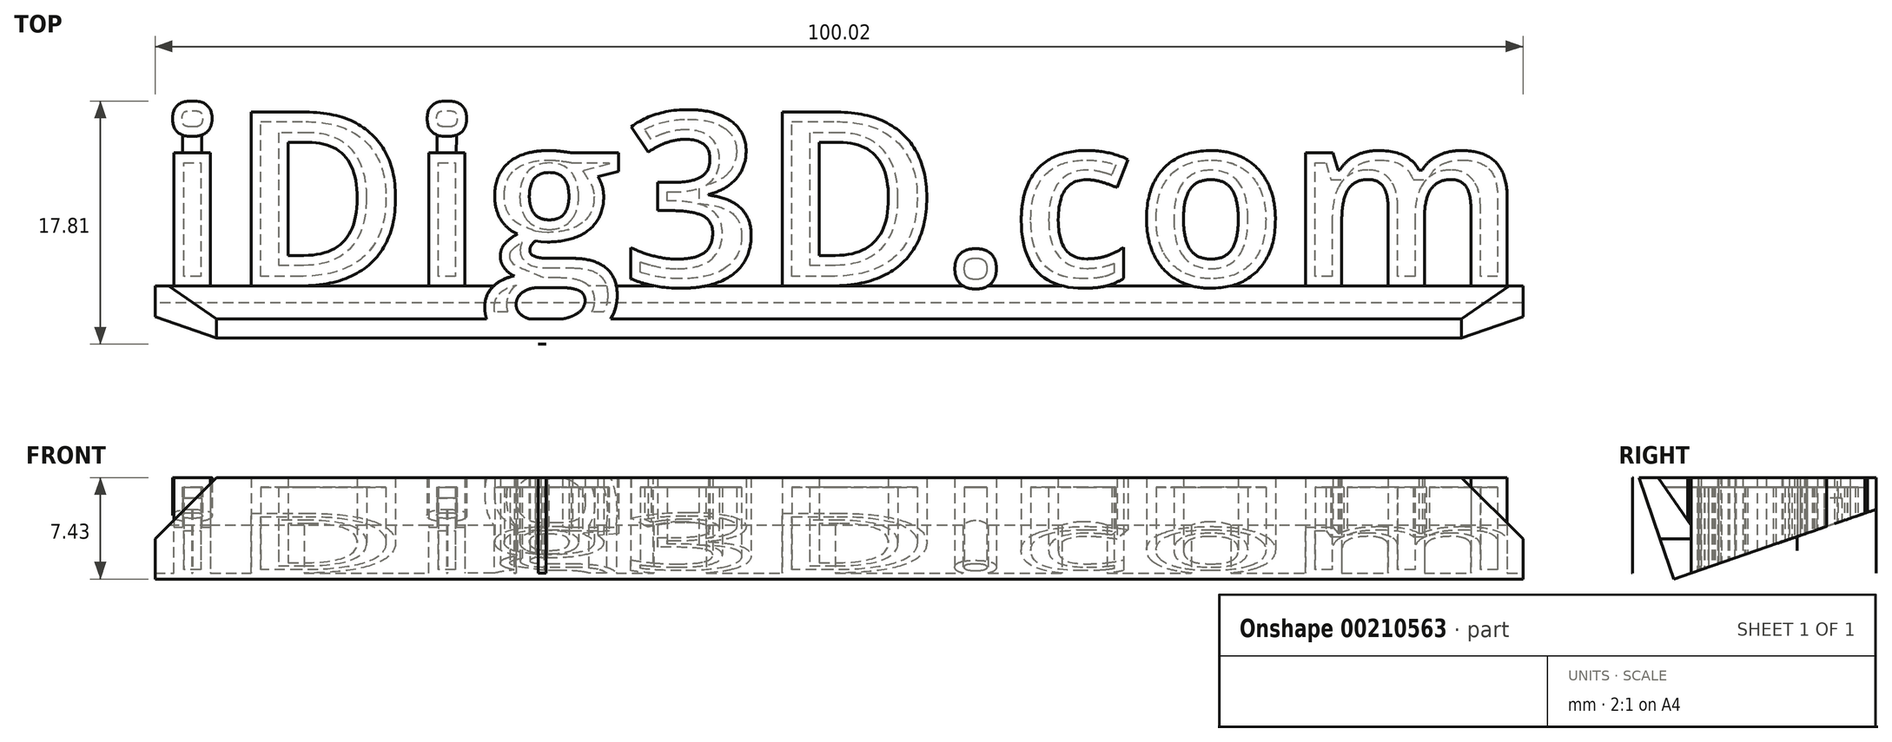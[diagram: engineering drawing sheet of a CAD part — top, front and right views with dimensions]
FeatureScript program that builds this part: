
annotation { "Feature Type Name" : "Feature", "Feature Type Description" : "" }
export const myFeature = defineFeature(function(context is Context, id is Id, definition is map)
    precondition{}
    {
        {
            var Q0;
            Q0=qCreatedBy(makeId("Top.planeOp"),FACE);
            var sketch = newSketch(context, id + "F0", { "sketchPlane" : qUnion([Q0])});
            skText(sketch, "E0", { "text": "iDig3D.com", "fontName": "OpenSans-Bold.ttf"});
            const initialGuessF0  = {"E0": [-0.05, -0.01282, 1, 0, 0.01282]};
            skSetInitialGuess(sketch, initialGuessF0);
            skSolve(sketch);
        }
        {
            var Q0;
            Q0=qSketchRegion(id+"F0",true);
            extrude(context, id + "F1", {"entities" : qUnion([Q0]), "depth" : 7 * mm});
        }
        {
            var Q0;
            Q0=makeQuery(id+"F0.imprint","IMPRINT",FACE,{"disambiguationData":[TD([[makeQuery(id+"F0.imprint","IMPRINT",EDGE,{"derivedFrom":sQuery(id+"F0.wireOp",EDGE,"E0.sketch_text.stroke-5")}),-1.0]])]});
            var sketch = newSketch(context, id + "F2", { "sketchPlane" : qUnion([Q0])});
            skPoint(sketch, "E1.0", {"position": v(-47.28, -3.1) * mm});
            skPoint(sketch, "E2.0", {"position": v(-28.67, -3.1) * mm});
            skPoint(sketch, "E3.0", {"position": v(-28.67, -1.9) * mm});
            skPoint(sketch, "E4.0", {"position": v(-47.28, -1.9) * mm});
            skLineSegment(sketch, "E5", {"start": v(-28.67, -1.9) * mm, "end": v(-28.67, -3.1) * mm});
            skLineSegment(sketch, "E6", {"start": v(-47.28, -1.9) * mm, "end": v(-47.28, -3.1) * mm});
            skArc(sketch, "E7.0.startCap", {"start": v(-29.37, -1.89) * mm, "mid": v(-28.67, -1.2) * mm, "end": v(-27.97, -1.9) * mm});
            skArc(sketch, "E7.0.endCap", {"start": v(-27.97, -3.1) * mm, "mid": v(-28.67, -3.8) * mm, "end": v(-29.37, -3.1) * mm});
            skLineSegment(sketch, "E7.0.left", {"start": v(-27.97, -1.9) * mm, "end": v(-27.97, -3.1) * mm});
            skLineSegment(sketch, "E7.0.right", {"start": v(-29.37, -1.89) * mm, "end": v(-29.37, -3.1) * mm});
            skArc(sketch, "E7.1.startCap", {"start": v(-47.98, -1.89) * mm, "mid": v(-47.28, -1.2) * mm, "end": v(-46.58, -1.9) * mm});
            skArc(sketch, "E7.1.endCap", {"start": v(-46.58, -3.1) * mm, "mid": v(-47.29, -3.8) * mm, "end": v(-47.98, -3.1) * mm});
            skLineSegment(sketch, "E7.1.left", {"start": v(-46.58, -1.9) * mm, "end": v(-46.58, -3.1) * mm});
            skLineSegment(sketch, "E7.1.right", {"start": v(-47.98, -1.89) * mm, "end": v(-47.98, -3.1) * mm});
            skSolve(sketch);
        }
        {
            var Q0;
            Q0=qSketchRegion(id+"F2",true);
            extrude(context, id + "F3", {"entities" : qUnion([Q0]), "operationType" : NewBodyOperationType.ADD, "depth" : 5.5 * mm});
        }
        {
            var Q0;
            Q0=makeQuery(id+"F1.opExtrude","CAP_FACE",FACE,{"disambiguationData":[OSD([sQuery(id+"F0.wireOp",EDGE,"E0.sketch_text.stroke-153"),sQuery(id+"F0.wireOp",EDGE,"E0.sketch_text.stroke-154"),sQuery(id+"F0.wireOp",EDGE,"E0.sketch_text.stroke-155"),sQuery(id+"F0.wireOp",EDGE,"E0.sketch_text.stroke-156"),sQuery(id+"F0.wireOp",EDGE,"E0.sketch_text.stroke-157"),sQuery(id+"F0.wireOp",EDGE,"E0.sketch_text.stroke-158"),sQuery(id+"F0.wireOp",EDGE,"E0.sketch_text.stroke-159"),sQuery(id+"F0.wireOp",EDGE,"E0.sketch_text.stroke-160"),sQuery(id+"F0.wireOp",EDGE,"E0.sketch_text.stroke-161"),sQuery(id+"F0.wireOp",EDGE,"E0.sketch_text.stroke-162"),sQuery(id+"F0.wireOp",EDGE,"E0.sketch_text.stroke-163"),sQuery(id+"F0.wireOp",EDGE,"E0.sketch_text.stroke-164"),sQuery(id+"F0.wireOp",EDGE,"E0.sketch_text.stroke-165"),sQuery(id+"F0.wireOp",EDGE,"E0.sketch_text.stroke-166"),sQuery(id+"F0.wireOp",EDGE,"E0.sketch_text.stroke-167"),sQuery(id+"F0.wireOp",EDGE,"E0.sketch_text.stroke-168"),sQuery(id+"F0.wireOp",EDGE,"E0.sketch_text.stroke-169"),sQuery(id+"F0.wireOp",EDGE,"E0.sketch_text.stroke-170"),sQuery(id+"F0.wireOp",EDGE,"E0.sketch_text.stroke-171"),sQuery(id+"F0.wireOp",EDGE,"E0.sketch_text.stroke-172"),sQuery(id+"F0.wireOp",EDGE,"E0.sketch_text.stroke-173"),sQuery(id+"F0.wireOp",EDGE,"E0.sketch_text.stroke-174"),sQuery(id+"F0.wireOp",EDGE,"E0.sketch_text.stroke-175"),sQuery(id+"F0.wireOp",EDGE,"E0.sketch_text.stroke-176"),sQuery(id+"F0.wireOp",EDGE,"E0.sketch_text.stroke-177"),sQuery(id+"F0.wireOp",EDGE,"E0.sketch_text.stroke-178"),sQuery(id+"F0.wireOp",EDGE,"E0.sketch_text.stroke-179"),sQuery(id+"F0.wireOp",EDGE,"E0.sketch_text.stroke-180")])],"isStart":true});
            var Q1;
            Q1=makeQuery(id+"F1.opExtrude","CAP_FACE",FACE,{"disambiguationData":[OSD([sQuery(id+"F0.wireOp",EDGE,"E0.sketch_text.stroke-30"),sQuery(id+"F0.wireOp",EDGE,"E0.sketch_text.stroke-31"),sQuery(id+"F0.wireOp",EDGE,"E0.sketch_text.stroke-32"),sQuery(id+"F0.wireOp",EDGE,"E0.sketch_text.stroke-33"),sQuery(id+"F0.wireOp",EDGE,"E0.sketch_text.stroke-34"),sQuery(id+"F0.wireOp",EDGE,"E0.sketch_text.stroke-35"),sQuery(id+"F0.wireOp",EDGE,"E0.sketch_text.stroke-36"),sQuery(id+"F0.wireOp",EDGE,"E0.sketch_text.stroke-37"),sQuery(id+"F0.wireOp",EDGE,"E0.sketch_text.stroke-38"),sQuery(id+"F0.wireOp",EDGE,"E0.sketch_text.stroke-39"),sQuery(id+"F0.wireOp",EDGE,"E0.sketch_text.stroke-40"),sQuery(id+"F0.wireOp",EDGE,"E0.sketch_text.stroke-41"),sQuery(id+"F0.wireOp",EDGE,"E0.sketch_text.stroke-42"),sQuery(id+"F0.wireOp",EDGE,"E0.sketch_text.stroke-43"),sQuery(id+"F0.wireOp",EDGE,"E0.sketch_text.stroke-44"),sQuery(id+"F0.wireOp",EDGE,"E0.sketch_text.stroke-45"),sQuery(id+"F0.wireOp",EDGE,"E0.sketch_text.stroke-46"),sQuery(id+"F0.wireOp",EDGE,"E0.sketch_text.stroke-47"),sQuery(id+"F0.wireOp",EDGE,"E0.sketch_text.stroke-48"),sQuery(id+"F0.wireOp",EDGE,"E0.sketch_text.stroke-49"),sQuery(id+"F0.wireOp",EDGE,"E0.sketch_text.stroke-50"),sQuery(id+"F0.wireOp",EDGE,"E0.sketch_text.stroke-51"),sQuery(id+"F0.wireOp",EDGE,"E0.sketch_text.stroke-52"),sQuery(id+"F0.wireOp",EDGE,"E0.sketch_text.stroke-53"),sQuery(id+"F0.wireOp",EDGE,"E0.sketch_text.stroke-54"),sQuery(id+"F0.wireOp",EDGE,"E0.sketch_text.stroke-55"),sQuery(id+"F0.wireOp",EDGE,"E0.sketch_text.stroke-56"),sQuery(id+"F0.wireOp",EDGE,"E0.sketch_text.stroke-57"),sQuery(id+"F0.wireOp",EDGE,"E0.sketch_text.stroke-58"),sQuery(id+"F0.wireOp",EDGE,"E0.sketch_text.stroke-59"),sQuery(id+"F0.wireOp",EDGE,"E0.sketch_text.stroke-60"),sQuery(id+"F0.wireOp",EDGE,"E0.sketch_text.stroke-61"),sQuery(id+"F0.wireOp",EDGE,"E0.sketch_text.stroke-62"),sQuery(id+"F0.wireOp",EDGE,"E0.sketch_text.stroke-63"),sQuery(id+"F0.wireOp",EDGE,"E0.sketch_text.stroke-64"),sQuery(id+"F0.wireOp",EDGE,"E0.sketch_text.stroke-65"),sQuery(id+"F0.wireOp",EDGE,"E0.sketch_text.stroke-66"),sQuery(id+"F0.wireOp",EDGE,"E0.sketch_text.stroke-67"),sQuery(id+"F0.wireOp",EDGE,"E0.sketch_text.stroke-68"),sQuery(id+"F0.wireOp",EDGE,"E0.sketch_text.stroke-69"),sQuery(id+"F0.wireOp",EDGE,"E0.sketch_text.stroke-70"),sQuery(id+"F0.wireOp",EDGE,"E0.sketch_text.stroke-71"),sQuery(id+"F0.wireOp",EDGE,"E0.sketch_text.stroke-72"),sQuery(id+"F0.wireOp",EDGE,"E0.sketch_text.stroke-73")])],"isStart":true});
            var Q2;
            Q2=makeQuery(id+"F1.opExtrude","CAP_FACE",FACE,{"disambiguationData":[OSD([sQuery(id+"F0.wireOp",EDGE,"E0.sketch_text.stroke-101"),sQuery(id+"F0.wireOp",EDGE,"E0.sketch_text.stroke-102"),sQuery(id+"F0.wireOp",EDGE,"E0.sketch_text.stroke-103"),sQuery(id+"F0.wireOp",EDGE,"E0.sketch_text.stroke-104"),sQuery(id+"F0.wireOp",EDGE,"E0.sketch_text.stroke-105"),sQuery(id+"F0.wireOp",EDGE,"E0.sketch_text.stroke-106"),sQuery(id+"F0.wireOp",EDGE,"E0.sketch_text.stroke-107"),sQuery(id+"F0.wireOp",EDGE,"E0.sketch_text.stroke-108"),sQuery(id+"F0.wireOp",EDGE,"E0.sketch_text.stroke-109"),sQuery(id+"F0.wireOp",EDGE,"E0.sketch_text.stroke-110"),sQuery(id+"F0.wireOp",EDGE,"E0.sketch_text.stroke-111"),sQuery(id+"F0.wireOp",EDGE,"E0.sketch_text.stroke-112")])],"isStart":true});
            var Q3;
            Q3=makeQuery(id+"F1.opExtrude","CAP_FACE",FACE,{"disambiguationData":[OSD([sQuery(id+"F0.wireOp",EDGE,"E0.sketch_text.stroke-0"),sQuery(id+"F0.wireOp",EDGE,"E0.sketch_text.stroke-1"),sQuery(id+"F0.wireOp",EDGE,"E0.sketch_text.stroke-2"),sQuery(id+"F0.wireOp",EDGE,"E0.sketch_text.stroke-3"),sQuery(id+"F0.wireOp",EDGE,"E0.sketch_text.stroke-4")])],"isStart":true});
            var Q4;
            Q4=makeQuery(id+"F1.opExtrude","CAP_FACE",FACE,{"disambiguationData":[OSD([sQuery(id+"F0.wireOp",EDGE,"E0.sketch_text.stroke-135"),sQuery(id+"F0.wireOp",EDGE,"E0.sketch_text.stroke-136"),sQuery(id+"F0.wireOp",EDGE,"E0.sketch_text.stroke-137"),sQuery(id+"F0.wireOp",EDGE,"E0.sketch_text.stroke-138"),sQuery(id+"F0.wireOp",EDGE,"E0.sketch_text.stroke-139"),sQuery(id+"F0.wireOp",EDGE,"E0.sketch_text.stroke-140"),sQuery(id+"F0.wireOp",EDGE,"E0.sketch_text.stroke-141"),sQuery(id+"F0.wireOp",EDGE,"E0.sketch_text.stroke-142"),sQuery(id+"F0.wireOp",EDGE,"E0.sketch_text.stroke-143"),sQuery(id+"F0.wireOp",EDGE,"E0.sketch_text.stroke-144"),sQuery(id+"F0.wireOp",EDGE,"E0.sketch_text.stroke-145"),sQuery(id+"F0.wireOp",EDGE,"E0.sketch_text.stroke-146"),sQuery(id+"F0.wireOp",EDGE,"E0.sketch_text.stroke-147"),sQuery(id+"F0.wireOp",EDGE,"E0.sketch_text.stroke-148"),sQuery(id+"F0.wireOp",EDGE,"E0.sketch_text.stroke-149"),sQuery(id+"F0.wireOp",EDGE,"E0.sketch_text.stroke-150"),sQuery(id+"F0.wireOp",EDGE,"E0.sketch_text.stroke-151"),sQuery(id+"F0.wireOp",EDGE,"E0.sketch_text.stroke-152")])],"isStart":true});
            var Q5;
            Q5=makeQuery(id+"F1.opExtrude","CAP_FACE",FACE,{"disambiguationData":[OSD([sQuery(id+"F0.wireOp",EDGE,"E0.sketch_text.stroke-121"),sQuery(id+"F0.wireOp",EDGE,"E0.sketch_text.stroke-122"),sQuery(id+"F0.wireOp",EDGE,"E0.sketch_text.stroke-123"),sQuery(id+"F0.wireOp",EDGE,"E0.sketch_text.stroke-124"),sQuery(id+"F0.wireOp",EDGE,"E0.sketch_text.stroke-125"),sQuery(id+"F0.wireOp",EDGE,"E0.sketch_text.stroke-126"),sQuery(id+"F0.wireOp",EDGE,"E0.sketch_text.stroke-127"),sQuery(id+"F0.wireOp",EDGE,"E0.sketch_text.stroke-128"),sQuery(id+"F0.wireOp",EDGE,"E0.sketch_text.stroke-129"),sQuery(id+"F0.wireOp",EDGE,"E0.sketch_text.stroke-130"),sQuery(id+"F0.wireOp",EDGE,"E0.sketch_text.stroke-131"),sQuery(id+"F0.wireOp",EDGE,"E0.sketch_text.stroke-132"),sQuery(id+"F0.wireOp",EDGE,"E0.sketch_text.stroke-133"),sQuery(id+"F0.wireOp",EDGE,"E0.sketch_text.stroke-134")])],"isStart":true});
            var Q6;
            Q6=makeQuery(id+"F1.opExtrude","CAP_FACE",FACE,{"disambiguationData":[OSD([sQuery(id+"F0.wireOp",EDGE,"E0.sketch_text.stroke-74"),sQuery(id+"F0.wireOp",EDGE,"E0.sketch_text.stroke-75"),sQuery(id+"F0.wireOp",EDGE,"E0.sketch_text.stroke-76"),sQuery(id+"F0.wireOp",EDGE,"E0.sketch_text.stroke-77"),sQuery(id+"F0.wireOp",EDGE,"E0.sketch_text.stroke-78"),sQuery(id+"F0.wireOp",EDGE,"E0.sketch_text.stroke-79"),sQuery(id+"F0.wireOp",EDGE,"E0.sketch_text.stroke-80"),sQuery(id+"F0.wireOp",EDGE,"E0.sketch_text.stroke-81"),sQuery(id+"F0.wireOp",EDGE,"E0.sketch_text.stroke-82"),sQuery(id+"F0.wireOp",EDGE,"E0.sketch_text.stroke-83"),sQuery(id+"F0.wireOp",EDGE,"E0.sketch_text.stroke-84"),sQuery(id+"F0.wireOp",EDGE,"E0.sketch_text.stroke-85"),sQuery(id+"F0.wireOp",EDGE,"E0.sketch_text.stroke-86"),sQuery(id+"F0.wireOp",EDGE,"E0.sketch_text.stroke-87"),sQuery(id+"F0.wireOp",EDGE,"E0.sketch_text.stroke-88"),sQuery(id+"F0.wireOp",EDGE,"E0.sketch_text.stroke-89"),sQuery(id+"F0.wireOp",EDGE,"E0.sketch_text.stroke-90"),sQuery(id+"F0.wireOp",EDGE,"E0.sketch_text.stroke-91"),sQuery(id+"F0.wireOp",EDGE,"E0.sketch_text.stroke-92"),sQuery(id+"F0.wireOp",EDGE,"E0.sketch_text.stroke-93"),sQuery(id+"F0.wireOp",EDGE,"E0.sketch_text.stroke-94"),sQuery(id+"F0.wireOp",EDGE,"E0.sketch_text.stroke-95"),sQuery(id+"F0.wireOp",EDGE,"E0.sketch_text.stroke-96"),sQuery(id+"F0.wireOp",EDGE,"E0.sketch_text.stroke-97"),sQuery(id+"F0.wireOp",EDGE,"E0.sketch_text.stroke-98"),sQuery(id+"F0.wireOp",EDGE,"E0.sketch_text.stroke-99"),sQuery(id+"F0.wireOp",EDGE,"E0.sketch_text.stroke-100")])],"isStart":true});
            var Q7;
            Q7=makeQuery(id+"F1.opExtrude","CAP_FACE",FACE,{"disambiguationData":[OSD([sQuery(id+"F0.wireOp",EDGE,"E0.sketch_text.stroke-21"),sQuery(id+"F0.wireOp",EDGE,"E0.sketch_text.stroke-22"),sQuery(id+"F0.wireOp",EDGE,"E0.sketch_text.stroke-23"),sQuery(id+"F0.wireOp",EDGE,"E0.sketch_text.stroke-24"),sQuery(id+"F0.wireOp",EDGE,"E0.sketch_text.stroke-25")])],"isStart":true});
            var Q8;
            Q8=makeQuery(id+"F1.opExtrude","CAP_FACE",FACE,{"disambiguationData":[OSD([sQuery(id+"F0.wireOp",EDGE,"E0.sketch_text.stroke-26"),sQuery(id+"F0.wireOp",EDGE,"E0.sketch_text.stroke-27"),sQuery(id+"F0.wireOp",EDGE,"E0.sketch_text.stroke-28"),sQuery(id+"F0.wireOp",EDGE,"E0.sketch_text.stroke-29")])],"isStart":true});
            var Q9;
            Q9=makeQuery(id+"F1.opExtrude","CAP_FACE",FACE,{"disambiguationData":[OSD([sQuery(id+"F0.wireOp",EDGE,"E0.sketch_text.stroke-9"),sQuery(id+"F0.wireOp",EDGE,"E0.sketch_text.stroke-10"),sQuery(id+"F0.wireOp",EDGE,"E0.sketch_text.stroke-11"),sQuery(id+"F0.wireOp",EDGE,"E0.sketch_text.stroke-12"),sQuery(id+"F0.wireOp",EDGE,"E0.sketch_text.stroke-13"),sQuery(id+"F0.wireOp",EDGE,"E0.sketch_text.stroke-14"),sQuery(id+"F0.wireOp",EDGE,"E0.sketch_text.stroke-15"),sQuery(id+"F0.wireOp",EDGE,"E0.sketch_text.stroke-16"),sQuery(id+"F0.wireOp",EDGE,"E0.sketch_text.stroke-17"),sQuery(id+"F0.wireOp",EDGE,"E0.sketch_text.stroke-18"),sQuery(id+"F0.wireOp",EDGE,"E0.sketch_text.stroke-19"),sQuery(id+"F0.wireOp",EDGE,"E0.sketch_text.stroke-20")])],"isStart":true});
            var Q10;
            Q10=makeQuery(id+"F1.opExtrude","CAP_FACE",FACE,{"disambiguationData":[OSD([sQuery(id+"F0.wireOp",EDGE,"E0.sketch_text.stroke-5"),sQuery(id+"F0.wireOp",EDGE,"E0.sketch_text.stroke-6"),sQuery(id+"F0.wireOp",EDGE,"E0.sketch_text.stroke-7"),sQuery(id+"F0.wireOp",EDGE,"E0.sketch_text.stroke-8")])],"isStart":true});
            var Q11;
            Q11=makeQuery(id+"F1.opExtrude","CAP_FACE",FACE,{"disambiguationData":[OSD([sQuery(id+"F0.wireOp",EDGE,"E0.sketch_text.stroke-113"),sQuery(id+"F0.wireOp",EDGE,"E0.sketch_text.stroke-114"),sQuery(id+"F0.wireOp",EDGE,"E0.sketch_text.stroke-115"),sQuery(id+"F0.wireOp",EDGE,"E0.sketch_text.stroke-116"),sQuery(id+"F0.wireOp",EDGE,"E0.sketch_text.stroke-117"),sQuery(id+"F0.wireOp",EDGE,"E0.sketch_text.stroke-118"),sQuery(id+"F0.wireOp",EDGE,"E0.sketch_text.stroke-119"),sQuery(id+"F0.wireOp",EDGE,"E0.sketch_text.stroke-120")])],"isStart":true});
            shell(context, id + "F4", {"entities" : qUnion([Q0, Q1, Q2, Q3, Q4, Q5, Q6, Q7, Q8, Q9, Q10, Q11]), "thickness" : .7 * mm});
        }
        {
            var Q0;
            Q0=qCreatedBy(makeId("Right.planeOp"),FACE);
            var sketch = newSketch(context, id + "F5", { "sketchPlane" : qUnion([Q0])});
            skPoint(sketch, "E8.0", {"position": v(0, 0) * mm});
            skPoint(sketch, "E8.1", {"position": v(-12.82, 0) * mm});
            skLineSegment(sketch, "E9.0", {"start": v(0.7, 7) * mm, "end": v(0.7, 4.67) * mm});
            skLineSegment(sketch, "E10.0", {"start": v(-17.1, 7) * mm, "end": v(-17.1, 0) * mm});
            skLineSegment(sketch, "E11", {"start": v(0.7, 4.67) * mm, "end": v(0.7, 2.33) * mm});
            skLineSegment(sketch, "E12", {"start": v(0.7, 2.33) * mm, "end": v(0.7, 0) * mm});
            skLineSegment(sketch, "E13", {"start": v(0.7, 4.67) * mm, "end": v(-14.07, -0.43) * mm});
            skLineSegment(sketch, "E14", {"start": v(-12.82, 0) * mm, "end": v(-15.23, 7) * mm, "construction": true});
            skLineSegment(sketch, "E15", {"start": v(-12.82, 7) * mm, "end": v(0.7, 7) * mm});
            skLineSegment(sketch, "E16", {"start": v(-12.82, 0) * mm, "end": v(-12.82, 7) * mm});
            skLineSegment(sketch, "E17", {"start": v(-15.23, 7) * mm, "end": v(-12.82, 3.5) * mm});
            skLineSegment(sketch, "E18", {"start": v(-14.07, -0.43) * mm, "end": v(-16.63, 7) * mm});
            skLineSegment(sketch, "E19", {"start": v(-16.63, 7) * mm, "end": v(-15.23, 7) * mm});
            skLineSegment(sketch, "E20", {"start": v(-16.63, 7) * mm, "end": v(-17.1, 7) * mm});
            skLineSegment(sketch, "E21", {"start": v(-17.1, 0) * mm, "end": v(-14.22, 0) * mm});
            skLineSegment(sketch, "E22.trimOffspring", {"start": v(-12.82, 0) * mm, "end": v(0.7, 0) * mm});
            skSolve(sketch);
        }
        {
            var Q0;
            Q0=makeQuery(id+"F5.imprint","IMPRINT",FACE,{"disambiguationData":[TD([[makeQuery(id+"F5.imprint","IMPRINT",EDGE,{"derivedFrom":sQuery(id+"F5.wireOp",EDGE,"E11")}),-1.0]])]});
            var Q1;
            {var subQ0=sQuery(id+"F5.wireOp",EDGE,"E10.0");Q1=makeQuery(id+"F5.imprint","IMPRINT",FACE,{"disambiguationData":[TD([[makeQuery(id+"F5.imprint","IMPRINT",EDGE,{"derivedFrom":subQ0}),1.0]])]});}
            var Q2;
            Q2=makeQuery(id+"F1.opExtrude","SWEPT_FACE",FACE,{"disambiguationData":[OSD([sQuery(id+"F0.wireOp",EDGE,"d4536f9c-434f-49d7-b92b-0fbf4eb391be.sketch_text.stroke-78")])]});
            var Q3;
            Q3=sQuery(id+"F0.wireOp",VERTEX,"E0.sketch_text.left.start");
            var Q4;
            Q4=makeQuery(id+"F1.opExtrude","SWEPT_FACE",FACE,{"disambiguationData":[OSD([sQuery(id+"F0.wireOp",EDGE,"d4536f9c-434f-49d7-b92b-0fbf4eb391be.sketch_text.stroke-15")])]});
            var Q5;
            Q5=sQuery(id+"F0.wireOp",VERTEX,"E0.sketch_text.right.start");
            extrude(context, id + "F6", {"entities" : qUnion([Q0, Q1]), "operationType" : NewBodyOperationType.REMOVE, "endBound" : BoundingType.UP_TO_VERTEX, "oppositeDirection" : true, "endBoundEntityFace" : qUnion([Q2]), "endBoundEntityVertex" : qUnion([Q3]), "depth" : 25 * mm, "hasSecondDirection" : true, "secondDirectionBound" : SecondDirectionBoundingType.UP_TO_VERTEX, "secondDirectionOppositeDirection" : false, "secondDirectionBoundEntityFace" : qUnion([Q4]), "secondDirectionBoundEntityVertex" : qUnion([Q5]), "secondDirectionDepth" : 25 * mm});
        }
        {
            var Q0;
            {var subQ1=sQuery(id+"F5.wireOp",EDGE,"E17");Q0=makeQuery(id+"F5.imprint","IMPRINT",FACE,{"disambiguationData":[TD([[makeQuery(id+"F5.imprint","IMPRINT",EDGE,{"derivedFrom":subQ1}),-1.0]])]});}
            var Q1;
            Q1=sQuery(id+"F0.wireOp",VERTEX,"E0.sketch_text.right.start");
            var Q2;
            Q2=makeQuery(id+"F1.opExtrude","SWEPT_FACE",FACE,{"disambiguationData":[OSD([sQuery(id+"F0.wireOp",EDGE,"d4536f9c-434f-49d7-b92b-0fbf4eb391be.sketch_text.stroke-15")])]});
            var Q3;
            Q3=sQuery(id+"F0.wireOp",VERTEX,"E0.sketch_text.left.start");
            extrude(context, id + "F7", {"entities" : qUnion([Q0]), "operationType" : NewBodyOperationType.ADD, "endBound" : BoundingType.UP_TO_VERTEX, "endBoundEntityVertex" : qUnion([Q1]), "depth" : 25 * mm, "hasSecondDirection" : true, "secondDirectionBound" : SecondDirectionBoundingType.UP_TO_VERTEX, "secondDirectionOppositeDirection" : true, "secondDirectionBoundEntityFace" : qUnion([Q2]), "secondDirectionBoundEntityVertex" : qUnion([Q3]), "secondDirectionDepth" : 25 * mm});
        }
        {
            var Q0;
            Q0=makeQuery(id+"F7.opExtrude","CAP_EDGE",EDGE,{"disambiguationData":[OSD([sQuery(id+"F5.wireOp",EDGE,"E19")])],"isStart":false});
            var Q1;
            Q1=makeQuery(id+"F7.opExtrude","CAP_EDGE",EDGE,{"disambiguationData":[OSD([sQuery(id+"F5.wireOp",EDGE,"E19")])],"isStart":true});
            chamfer(context, id + "F8", {"entities" : qUnion([Q0, Q1]), "width" : 4.5 * mm, "tangentPropagation" : true});
        }
    });
